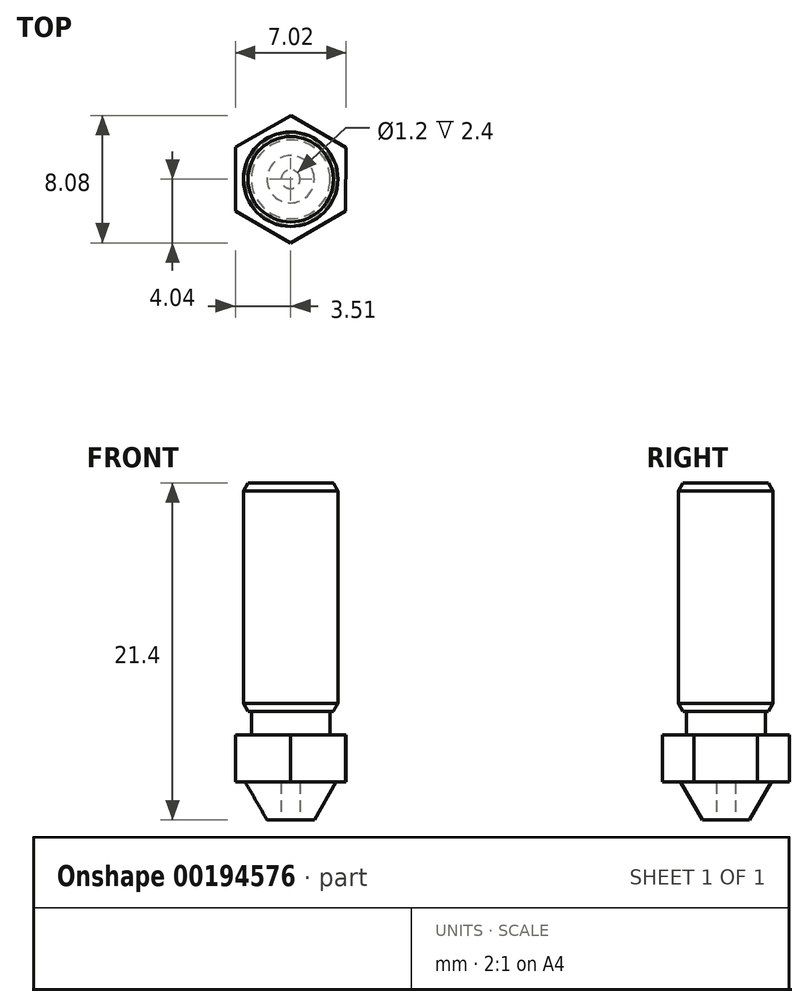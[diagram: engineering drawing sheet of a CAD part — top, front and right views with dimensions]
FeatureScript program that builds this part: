
annotation { "Feature Type Name" : "Feature", "Feature Type Description" : "" }
export const myFeature = defineFeature(function(context is Context, id is Id, definition is map)
    precondition{}
    {
        {
            var Q0;
            Q0=qCreatedBy(makeId("Front.planeOp"),FACE);
            var sketch = newSketch(context, id + "F0", { "sketchPlane" : qUnion([Q0])});
            skLineSegment(sketch, "E0", {"start": v(0, 0) * mm, "end": v(0.9, 0) * mm});
            skLineSegment(sketch, "E1", {"start": v(0.9, 0) * mm, "end": v(2.29, 2.4) * mm});
            skLineSegment(sketch, "E2", {"start": v(2.29, 2.4) * mm, "end": v(0, 2.4) * mm});
            skLineSegment(sketch, "E3", {"start": v(-0.6, 0) * mm, "end": v(-0.6, 2.4) * mm, "construction": true});
            skLineSegment(sketch, "E4", {"start": v(0, 0) * mm, "end": v(0, 2.4) * mm});
            skSolve(sketch);
        }
        {
            var Q0;
            Q0 = qSketchRegion(id + "F0", true);
            var Q1;
            Q1=sQuery(id+"F0.wireOp",EDGE,"E3");
            revolve(context, id + "F1", {"entities" : qUnion([Q0]), "axis" : qUnion([Q1]), "revolveType" : RevolveType.FULL});
        }
        {
            var Q0;
            Q0=makeQuery(id+"F1.opRevolve","SWEPT_FACE",FACE,{"disambiguationData":[OSD([sQuery(id+"F0.wireOp",EDGE,"E2")])]});
            var sketch = newSketch(context, id + "F2", { "sketchPlane" : qUnion([Q0])});
            skCircle(sketch, "E5.cCircle", {"center": v(-0.6, 0) * mm, "radius": 3.5 * mm, "construction": true});
            skLineSegment(sketch, "E5.0", {"start": v(-0.59, 4.04) * mm, "end": v(2.9, 2) * mm});
            skLineSegment(sketch, "E5.1", {"start": v(2.9, 2) * mm, "end": v(2.9, -2.03) * mm});
            skLineSegment(sketch, "E5.2", {"start": v(2.9, -2.03) * mm, "end": v(-0.61, -4.04) * mm});
            skLineSegment(sketch, "E5.3", {"start": v(-0.61, -4.04) * mm, "end": v(-4.1, -2) * mm});
            skLineSegment(sketch, "E5.4", {"start": v(-4.1, -2) * mm, "end": v(-4.1, 2.03) * mm});
            skLineSegment(sketch, "E5.5", {"start": v(-4.1, 2.03) * mm, "end": v(-0.59, 4.04) * mm});
            skPoint(sketch, "E5.0.midPoint", {"position": v(1.16, 3.02) * mm});
            skSolve(sketch);
        }
        {
            var Q0;
            Q0 = qSketchRegion(id + "F2", true);
            extrude(context, id + "F3", {"entities" : qUnion([Q0]), "operationType" : NewBodyOperationType.ADD, "depth" : 3 * mm});
        }
        {
            var Q0;
            Q0=makeQuery(id+"F3.opExtrude","CAP_FACE",FACE,{"disambiguationData":[OSD([sQuery(id+"F2.wireOp",EDGE,"E5.0"),sQuery(id+"F2.wireOp",EDGE,"E5.1"),sQuery(id+"F2.wireOp",EDGE,"E5.2"),sQuery(id+"F2.wireOp",EDGE,"E5.3"),sQuery(id+"F2.wireOp",EDGE,"E5.4"),sQuery(id+"F2.wireOp",EDGE,"E5.5")])],"isStart":false});
            var sketch = newSketch(context, id + "F4", { "sketchPlane" : qUnion([Q0])});
            skCircle(sketch, "E6", {"center": v(-0.6, 0) * mm, "radius": 2.5 * mm});
            skSolve(sketch);
        }
        {
            var Q0;
            Q0 = qSketchRegion(id + "F4", true);
            extrude(context, id + "F5", {"entities" : qUnion([Q0]), "operationType" : NewBodyOperationType.ADD, "depth" : 1.5 * mm});
        }
        {
            var Q0;
            Q0=makeQuery(id+"F5.opExtrude","CAP_FACE",FACE,{"disambiguationData":[OSD([sQuery(id+"F4.wireOp",EDGE,"E6")])],"isStart":false});
            var sketch = newSketch(context, id + "F6", { "sketchPlane" : qUnion([Q0])});
            skCircle(sketch, "E7", {"center": v(-0.6, 0) * mm, "radius": 3 * mm});
            skSolve(sketch);
        }
        {
            var Q0;
            Q0 = qSketchRegion(id + "F6", true);
            extrude(context, id + "F7", {"entities" : qUnion([Q0]), "operationType" : NewBodyOperationType.ADD, "depth" : 14.5 * mm});
        }
        {
            var Q0;
            Q0=makeQuery(id+"F7.opExtrude","CAP_EDGE",EDGE,{"disambiguationData":[OSD([sQuery(id+"F6.wireOp",EDGE,"E7")])],"isStart":false});
            var Q1;
            Q1=makeQuery(id+"F7.opExtrude","CAP_EDGE",EDGE,{"disambiguationData":[OSD([sQuery(id+"F6.wireOp",EDGE,"E7")])],"isStart":true});
            chamfer(context, id + "F8", {"entities" : qUnion([Q0, Q1]), "chamferType" : ChamferType.OFFSET_ANGLE, "width" : 0.5 * mm, "oppositeDirection" : false, "angle" : 30 * degree, "tangentPropagation" : true});
        }
    });
